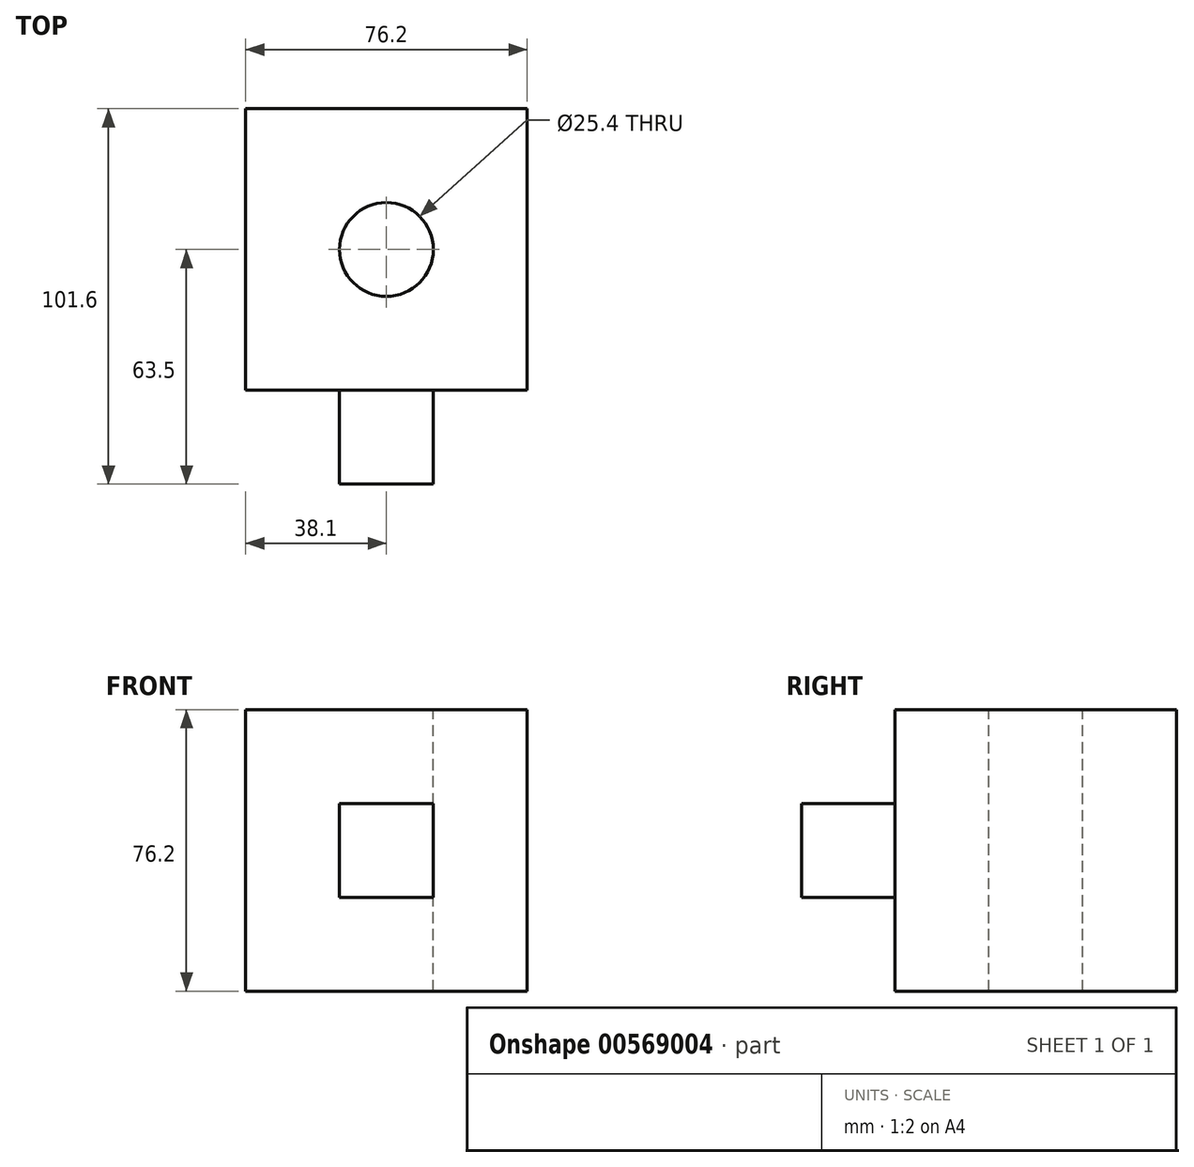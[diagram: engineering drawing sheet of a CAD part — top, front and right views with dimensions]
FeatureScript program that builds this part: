
annotation { "Feature Type Name" : "Feature", "Feature Type Description" : "" }
export const myFeature = defineFeature(function(context is Context, id is Id, definition is map)
    precondition{}
    {
        {
            var Q0;
            Q0=qCreatedBy(makeId("Front.planeOp"),FACE);
            var sketch = newSketch(context, id + "F0", { "sketchPlane" : qUnion([Q0])});
            skLineSegment(sketch, "E0.bottom", {"start": v(0, 0) * mm, "end": v(76.2, 0) * mm});
            skLineSegment(sketch, "E0.top", {"start": v(0, 76.2) * mm, "end": v(76.2, 76.2) * mm});
            skLineSegment(sketch, "E0.left", {"start": v(0, 0) * mm, "end": v(0, 76.2) * mm});
            skLineSegment(sketch, "E0.right", {"start": v(76.2, 0) * mm, "end": v(76.2, 76.2) * mm});
            skSolve(sketch);
        }
        {
            var Q0;
            Q0 = qSketchRegion(id + "F0", true);
            extrude(context, id + "F1", {"entities" : qUnion([Q0]), "depth" : 76.2 * mm, "offsetDistance" : 25.4 * mm});
        }
        {
            var Q0;
            Q0=makeQuery(id+"F1.opExtrude","CAP_FACE",FACE,{"disambiguationData":[OSD([sQuery(id+"F0.wireOp",EDGE,"E0.bottom"),sQuery(id+"F0.wireOp",EDGE,"E0.top"),sQuery(id+"F0.wireOp",EDGE,"E0.left"),sQuery(id+"F0.wireOp",EDGE,"E0.right")])],"isStart":false});
            var sketch = newSketch(context, id + "F2", { "sketchPlane" : qUnion([Q0])});
            skLineSegment(sketch, "E1.bottom", {"start": v(25.4, 50.8) * mm, "end": v(50.8, 50.8) * mm});
            skLineSegment(sketch, "E1.top", {"start": v(25.4, 25.4) * mm, "end": v(50.8, 25.4) * mm});
            skLineSegment(sketch, "E1.left", {"start": v(25.4, 50.8) * mm, "end": v(25.4, 25.4) * mm});
            skLineSegment(sketch, "E1.right", {"start": v(50.8, 50.8) * mm, "end": v(50.8, 25.4) * mm});
            skSolve(sketch);
        }
        {
            var Q0;
            Q0=makeQuery(id+"F2.imprint","IMPRINT",FACE,{"disambiguationData":[TD([[makeQuery(id+"F2.imprint","IMPRINT",EDGE,{"derivedFrom":sQuery(id+"F2.wireOp",EDGE,"E1.bottom")}),-1.0]])]});
            extrude(context, id + "F3", {"entities" : qUnion([Q0]), "operationType" : NewBodyOperationType.ADD, "depth" : 25.4 * mm, "offsetDistance" : 25.4 * mm});
        }
        {
            var Q0;
            Q0=makeQuery(id+"F1.opExtrude","SWEPT_FACE",FACE,{"disambiguationData":[OSD([sQuery(id+"F0.wireOp",EDGE,"E0.top")])]});
            var sketch = newSketch(context, id + "F4", { "sketchPlane" : qUnion([Q0])});
            skPoint(sketch, "E2", {"position": v(38.1, -38.1) * mm});
            skSolve(sketch);
        }
        {
            var Q0;
            Q0=sQuery(id+"F4.wireOp",VERTEX,"E2");
            var Q1;
            Q1=makeQuery(id+"F1.opExtrude","SWEPT_BODY",BODY,{"disambiguationData":[OSD([sQuery(id+"F0.wireOp",EDGE,"E0.bottom"),sQuery(id+"F0.wireOp",EDGE,"E0.top"),sQuery(id+"F0.wireOp",EDGE,"E0.left"),sQuery(id+"F0.wireOp",EDGE,"E0.right")])]});
            hole(context, id + "F5", {"style" : HoleStyle.SIMPLE, "endStyle" : HoleEndStyle.THROUGH, "holeDiameter" : 25.4 * mm, "isTappedThrough" : true, "tappedDepth" : 12.7 * mm, "tapClearance" : 3, "locations" : qUnion([Q0]), "scope" : qUnion([Q1])});
        }
        {
            var Q0;
            Q0=makeQuery(id+"F1.opExtrude","SWEPT_FACE",FACE,{"disambiguationData":[OSD([sQuery(id+"F0.wireOp",EDGE,"E0.right")])]});
            var sketch = newSketch(context, id + "F6", { "sketchPlane" : qUnion([Q0])});
            skSolve(sketch);
        }
        {
            var Q0;
            {var subQ0=sQuery(id+"F0.wireOp",EDGE,"E0.right");Q0=makeQuery(id+"F6.imprint","IMPRINT",FACE,{"disambiguationData":[TD([[makeQuery(id+"F6.imprint","IMPRINT",EDGE,{"derivedFrom":makeQuery(id+"F1.opExtrude","CAP_EDGE",EDGE,{"disambiguationData":[OSD([subQ0])],"isStart":true})}),1.0]])]});}
            var sketch = newSketch(context, id + "F7", { "sketchPlane" : qUnion([Q0])});
            skCircle(sketch, "E3", {"center": v(-39.84, 38.8) * mm, "radius": 12.7 * mm});
            skSolve(sketch);
        }
        {
            var Q0;
            Q0=sQuery(id+"F7.wireOp",EDGE,"E3");
            extrude(context, id + "F8", {"bodyType" : ToolBodyType.SURFACE, "surfaceEntities" : qUnion([Q0]), "depth" : 12.7 * mm, "offsetDistance" : 25.4 * mm});
        }
    });
